# Revit family: Plumbing Fixture-FloorDrain_Mifab_C1100-RFC
name_source: partatom
category: Plumbing Fixtures
revit_build: Autodesk Revit Structure 2013 (Build: 20120221_2030(x64)
units: mm (PartAtom-declared; Revit-internal decimal feet)

## types (8) — shared parameters
Body Height = 2.75 "
Floor Drain Material = Paint - Sherwin Williams Paint - #952C2A - Bellwood Red
Manufacturer = MIFAB
Model = C1100-RFC
Top Assembly Height = 1.65 "
URL = WWW.MIFAB.COM
zero-valued in all types: Default Elevation, WFU

## per-type parameters (varying)
| type | Description | Pipe Diameter | Pipe Radius | Stainer Diameter | Strainer Radius |
| 2" FOR 7" | FLOOR CLEANOUT WITH SURFACE MEMBRANE CLAMP  ADJUSTABLE COVER AND PLUG | 2 " | 1 " | 7 " | 3.5 " |
| 3" FOR 7" | FLOOR CLEANOUT WITH SURFACE MEMBRANE CLAMP, ADJUSTABLE COVER AND PLUG | 3 " | 1.5 " | 7 " | 3.5 " |
| 4" FOR 7" | FLOOR CLEANOUT WITH SURFACE MEMBRANE CLAMP, ADJUSTABLE COVER AND PLUG | 4 " | 2 " | 7 " | 3.5 " |
| 5" FOR 7" | FLOOR CLEANOUT WITH SURFACE MEMBRANE CLAMP, ADJUSTABLE COVER AND PLUG | 5 " | 2.5 " | 7 " | 3.5 " |
| 2" FOR 9" | FLOOR CLEANOUT WITH SURFACE MEMBRANE
CLAMP, ADJUSTABLE COVER AND PLUG | 2 " | 1 " | 9 " | 4.5 " |
| 3" FOR 9" | FLOOR CLEANOUT WITH SURFACE MEMBRANE
CLAMP, ADJUSTABLE COVER AND PLUG | 3 " | 1.5 " | 9 " | 4.5 " |
| 4" FOR 9" | FLOOR CLEANOUT WITH SURFACE MEMBRANE CLAMP ADJUSTABLE COVER AND PLUG | 4 " | 2 " | 9 " | 4.5 " |
| 5" FOR 9" | FLOOR CLEANOUT WITH SURFACE MEMBRANE CLAMP, ADJUSTABLE COVER AND PLUG | 5 " | 2.5 " | 9 " | 4.5 " |

## geometry (parser evidence)
native form markers: Blend x3, Sweep x1
no freeform markers — native parametric forms only
